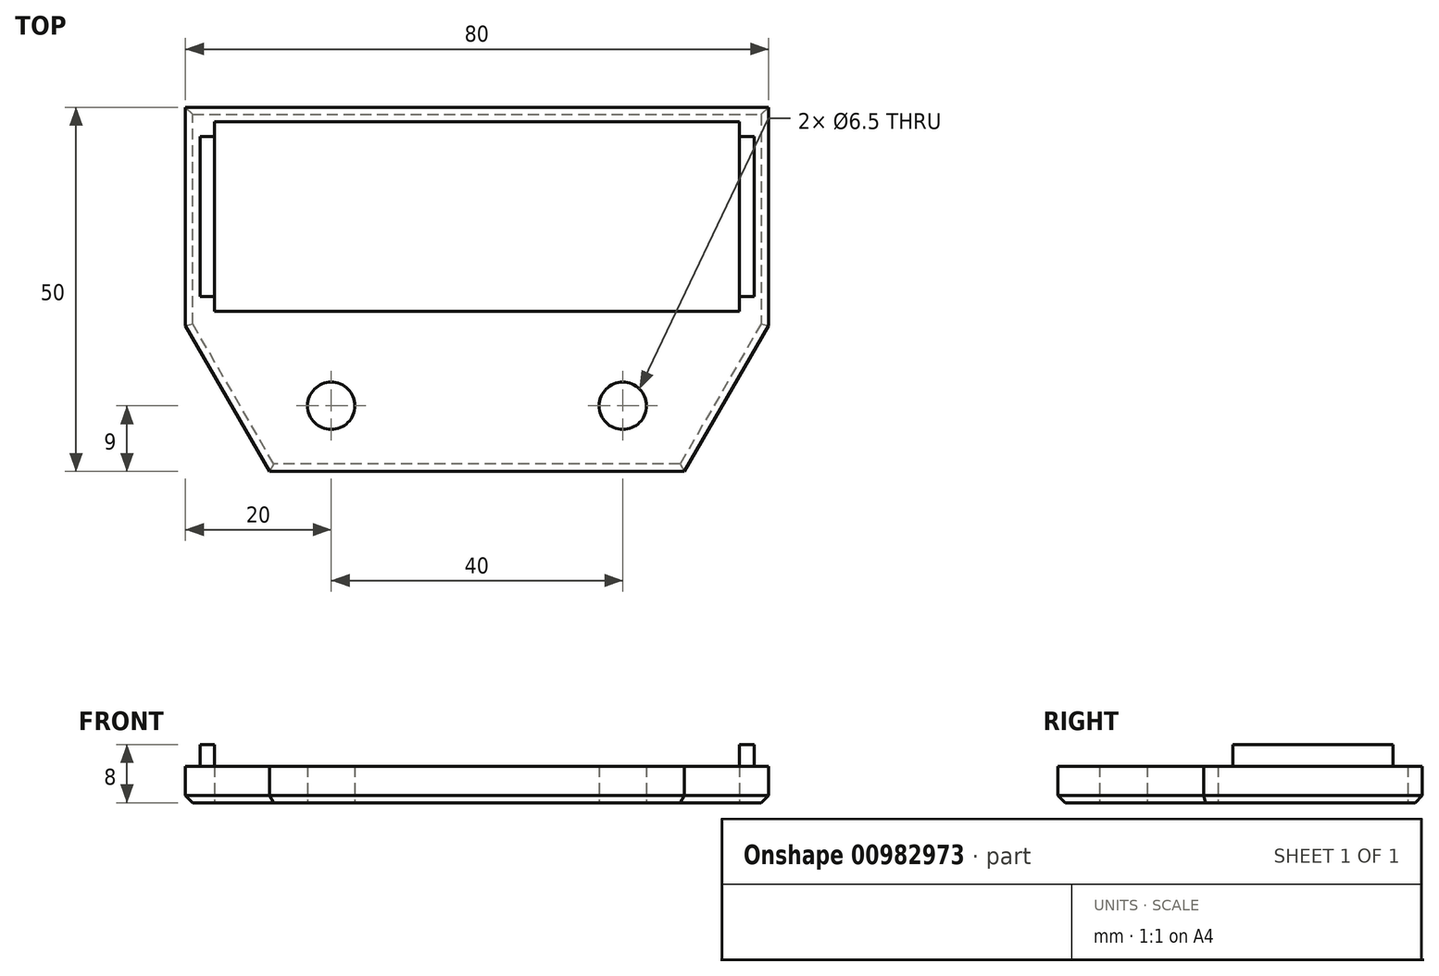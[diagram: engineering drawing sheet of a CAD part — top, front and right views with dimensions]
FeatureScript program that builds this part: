
annotation { "Feature Type Name" : "Feature", "Feature Type Description" : "" }
export const myFeature = defineFeature(function(context is Context, id is Id, definition is map)
    precondition{}
    {
        {
            var Q0;
            Q0=qCreatedBy(makeId("Top.planeOp"),FACE);
            var sketch = newSketch(context, id + "F0", { "sketchPlane" : qUnion([Q0])});
            skLineSegment(sketch, "E0.bottom", {"start": v(40, 15) * mm, "end": v(-40, 15) * mm});
            skLineSegment(sketch, "E0.top", {"start": v(40, -15) * mm, "end": v(-40, -15) * mm});
            skLineSegment(sketch, "E0.left", {"start": v(40, 15) * mm, "end": v(40, -15) * mm});
            skLineSegment(sketch, "E0.right", {"start": v(-40, 15) * mm, "end": v(-40, -15) * mm});
            skPoint(sketch, "E0.middle", {"position": v(0, 0) * mm});
            skLineSegment(sketch, "E1.bottom", {"start": v(36, 13) * mm, "end": v(-36, 13) * mm});
            skLineSegment(sketch, "E1.top", {"start": v(36, -13) * mm, "end": v(-36, -13) * mm});
            skLineSegment(sketch, "E1.left", {"start": v(36, 13) * mm, "end": v(36, -13) * mm});
            skLineSegment(sketch, "E1.right", {"start": v(-36, 13) * mm, "end": v(-36, -13) * mm});
            skSolve(sketch);
        }
        {
            var Q0;
            Q0=makeQuery(id+"F0.imprint","IMPRINT",FACE,{"disambiguationData":[TD([[makeQuery(id+"F0.imprint","IMPRINT",EDGE,{"derivedFrom":sQuery(id+"F0.wireOp",EDGE,"E0.bottom")}),1.0]])]});
            extrude(context, id + "F1", {"entities" : qUnion([Q0]), "depth" : 5 * mm, "offsetDistance" : 25 * mm});
        }
        {
            var Q0;
            Q0=makeQuery(id+"F1.opExtrude","CAP_FACE",FACE,{"disambiguationData":[OSD([sQuery(id+"F0.wireOp",EDGE,"E0.bottom"),sQuery(id+"F0.wireOp",EDGE,"E0.top"),sQuery(id+"F0.wireOp",EDGE,"E0.left"),sQuery(id+"F0.wireOp",EDGE,"E0.right"),sQuery(id+"F0.wireOp",EDGE,"E1.bottom"),sQuery(id+"F0.wireOp",EDGE,"E1.top"),sQuery(id+"F0.wireOp",EDGE,"E1.left"),sQuery(id+"F0.wireOp",EDGE,"E1.right")])],"isStart":false});
            var sketch = newSketch(context, id + "F2", { "sketchPlane" : qUnion([Q0])});
            skLineSegment(sketch, "E2", {"start": v(-36, 0) * mm, "end": v(-40, 0) * mm, "construction": true});
            skLineSegment(sketch, "E3.MirrorCS", {"start": v(36, 13) * mm, "end": v(36, 11) * mm});
            skLineSegment(sketch, "E4.bottom", {"start": v(-36, 11) * mm, "end": v(-38, 11) * mm});
            skLineSegment(sketch, "E4.top", {"start": v(-36, -11) * mm, "end": v(-38, -11) * mm});
            skLineSegment(sketch, "E4.left", {"start": v(-36, 11) * mm, "end": v(-36, -11) * mm});
            skLineSegment(sketch, "E4.right", {"start": v(-38, 11) * mm, "end": v(-38, -11) * mm});
            skLineSegment(sketch, "E5.MirrorCS", {"start": v(38, 11) * mm, "end": v(38, -11) * mm});
            skLineSegment(sketch, "E6.MirrorCS", {"start": v(36, 11) * mm, "end": v(36, -11) * mm});
            skLineSegment(sketch, "E7.MirrorCS", {"start": v(36, -11) * mm, "end": v(38, -11) * mm});
            skLineSegment(sketch, "E8.MirrorCS", {"start": v(36, 11) * mm, "end": v(38, 11) * mm});
            skSolve(sketch);
        }
        {
            var Q0;
            Q0 = qSketchRegion(id + "F2", true);
            extrude(context, id + "F3", {"entities" : qUnion([Q0]), "operationType" : NewBodyOperationType.ADD, "depth" : 3 * mm, "offsetDistance" : 25 * mm});
        }
        {
            var Q0;
            Q0=makeQuery(id+"F1.opExtrude","CAP_FACE",FACE,{"disambiguationData":[OSD([sQuery(id+"F0.wireOp",EDGE,"E0.bottom"),sQuery(id+"F0.wireOp",EDGE,"E0.top"),sQuery(id+"F0.wireOp",EDGE,"E0.left"),sQuery(id+"F0.wireOp",EDGE,"E0.right"),sQuery(id+"F0.wireOp",EDGE,"E1.bottom"),sQuery(id+"F0.wireOp",EDGE,"E1.top"),sQuery(id+"F0.wireOp",EDGE,"E1.left"),sQuery(id+"F0.wireOp",EDGE,"E1.right")])],"isStart":false});
            var sketch = newSketch(context, id + "F4", { "sketchPlane" : qUnion([Q0])});
            skLineSegment(sketch, "E9.bottom", {"start": v(-40, -15) * mm, "end": v(40, -15) * mm});
            skLineSegment(sketch, "E9.top", {"start": v(-40, -35) * mm, "end": v(40, -35) * mm});
            skLineSegment(sketch, "E9.left", {"start": v(-40, -15) * mm, "end": v(-40, -35) * mm});
            skLineSegment(sketch, "E9.right", {"start": v(40, -15) * mm, "end": v(40, -35) * mm});
            skLineSegment(sketch, "E10", {"start": v(-40, -15) * mm, "end": v(-28.45, -35) * mm});
            skLineSegment(sketch, "E11", {"start": v(40, -15) * mm, "end": v(28.45, -35) * mm});
            skSolve(sketch);
        }
        {
            var Q0;
            Q0=makeQuery(id+"F4.imprint","IMPRINT",FACE,{"disambiguationData":[TD([[makeQuery(id+"F4.imprint","IMPRINT",EDGE,{"derivedFrom":sQuery(id+"F4.wireOp",EDGE,"E9.bottom")}),1.0]])]});
            extrude(context, id + "F5", {"entities" : qUnion([Q0]), "operationType" : NewBodyOperationType.ADD, "oppositeDirection" : true, "depth" : 5 * mm, "offsetDistance" : 25 * mm});
        }
        {
            var Q0;
            Q0=makeQuery(id+"F1.opExtrude","CAP_EDGE",EDGE,{"disambiguationData":[OSD([sQuery(id+"F0.wireOp",EDGE,"E0.bottom")])],"isStart":true});
            var Q1;
            Q1=makeQuery(id+"F1.opExtrude","CAP_EDGE",EDGE,{"disambiguationData":[OSD([sQuery(id+"F0.wireOp",EDGE,"E0.right")])],"isStart":true});
            var Q2;
            Q2=makeQuery(id+"F1.opExtrude","CAP_EDGE",EDGE,{"disambiguationData":[OSD([sQuery(id+"F0.wireOp",EDGE,"E0.left")])],"isStart":true});
            var Q3;
            Q3=makeQuery(id+"F5.opExtrude","CAP_EDGE",EDGE,{"disambiguationData":[OSD([sQuery(id+"F4.wireOp",EDGE,"E11")])],"isStart":false});
            var Q4;
            Q4=makeQuery(id+"F5.opExtrude","CAP_EDGE",EDGE,{"disambiguationData":[OSD([sQuery(id+"F4.wireOp",EDGE,"E9.top")])],"isStart":false});
            var Q5;
            Q5=makeQuery(id+"F5.opExtrude","CAP_EDGE",EDGE,{"disambiguationData":[OSD([sQuery(id+"F4.wireOp",EDGE,"E10")])],"isStart":false});
            chamfer(context, id + "F6", {"entities" : qUnion([Q0, Q1, Q2, Q3, Q4, Q5]), "width" : 1 * mm, "tangentPropagation" : true});
        }
        {
            var Q0;
            Q0=makeQuery(id+"F5.boolean.opBoolean","MERGE",FACE,{"derivedFrom":[makeQuery(id+"F1.opExtrude","CAP_FACE",FACE,{"disambiguationData":[OSD([sQuery(id+"F0.wireOp",EDGE,"E0.bottom"),sQuery(id+"F0.wireOp",EDGE,"E0.top"),sQuery(id+"F0.wireOp",EDGE,"E0.left"),sQuery(id+"F0.wireOp",EDGE,"E0.right"),sQuery(id+"F0.wireOp",EDGE,"E1.bottom"),sQuery(id+"F0.wireOp",EDGE,"E1.top"),sQuery(id+"F0.wireOp",EDGE,"E1.left"),sQuery(id+"F0.wireOp",EDGE,"E1.right")])],"isStart":true}),makeQuery(id+"F5.opExtrude","CAP_FACE",FACE,{"disambiguationData":[OSD([sQuery(id+"F4.wireOp",EDGE,"E9.bottom"),sQuery(id+"F4.wireOp",EDGE,"E9.top"),sQuery(id+"F4.wireOp",EDGE,"E10"),sQuery(id+"F4.wireOp",EDGE,"E11")])],"isStart":false})]});
            var sketch = newSketch(context, id + "F7", { "sketchPlane" : qUnion([Q0])});
            skLineSegment(sketch, "E12", {"start": v(36, 13) * mm, "end": v(-36, 13) * mm, "construction": true});
            skLineSegment(sketch, "E13", {"start": v(-36, 13) * mm, "end": v(0, 13) * mm, "construction": true});
            skLineSegment(sketch, "E14", {"start": v(0, 13) * mm, "end": v(0, 34) * mm, "construction": true});
            skLineSegment(sketch, "E15", {"start": v(0, 34) * mm, "end": v(0, 26) * mm, "construction": true});
            skLineSegment(sketch, "E16", {"start": v(0, 26) * mm, "end": v(-20, 26) * mm, "construction": true});
            skLineSegment(sketch, "E17", {"start": v(0, 26) * mm, "end": v(20, 26) * mm, "construction": true});
            skCircle(sketch, "E18", {"center": v(20, 26) * mm, "radius": 1.65 * mm});
            skCircle(sketch, "E19", {"center": v(-20, 26) * mm, "radius": 1.65 * mm});
            skSolve(sketch);
        }
        {
            var Q0;
            Q0=sQuery(id+"F7.wireOp",VERTEX,"E17.end");
            var Q1;
            Q1=makeQuery(id+"F1.opExtrude","SWEPT_BODY",BODY,{"disambiguationData":[OSD([sQuery(id+"F0.wireOp",EDGE,"E0.bottom"),sQuery(id+"F0.wireOp",EDGE,"E0.top"),sQuery(id+"F0.wireOp",EDGE,"E0.left"),sQuery(id+"F0.wireOp",EDGE,"E0.right"),sQuery(id+"F0.wireOp",EDGE,"E1.bottom"),sQuery(id+"F0.wireOp",EDGE,"E1.top"),sQuery(id+"F0.wireOp",EDGE,"E1.left"),sQuery(id+"F0.wireOp",EDGE,"E1.right")])]});
            hole(context, id + "F8", {"style" : HoleStyle.SIMPLE, "endStyle" : HoleEndStyle.THROUGH, "holeDiameter" : 6.5 * mm, "majorDiameter" : 5 * mm, "isTappedThrough" : true, "tappedDepth" : 12 * mm, "tapClearance" : 3, "locations" : qUnion([Q0]), "scope" : qUnion([Q1])});
        }
        {
            var Q0;
            Q0=sQuery(id+"F7.wireOp",VERTEX,"E16.end");
            var Q1;
            Q1=makeQuery(id+"F1.opExtrude","SWEPT_BODY",BODY,{"disambiguationData":[OSD([sQuery(id+"F0.wireOp",EDGE,"E0.bottom"),sQuery(id+"F0.wireOp",EDGE,"E0.top"),sQuery(id+"F0.wireOp",EDGE,"E0.left"),sQuery(id+"F0.wireOp",EDGE,"E0.right"),sQuery(id+"F0.wireOp",EDGE,"E1.bottom"),sQuery(id+"F0.wireOp",EDGE,"E1.top"),sQuery(id+"F0.wireOp",EDGE,"E1.left"),sQuery(id+"F0.wireOp",EDGE,"E1.right")])]});
            hole(context, id + "F9", {"style" : HoleStyle.SIMPLE, "endStyle" : HoleEndStyle.THROUGH, "holeDiameter" : 6.5 * mm, "majorDiameter" : 5 * mm, "isTappedThrough" : true, "tappedDepth" : 12 * mm, "tapClearance" : 3, "locations" : qUnion([Q0]), "scope" : qUnion([Q1])});
        }
    });
